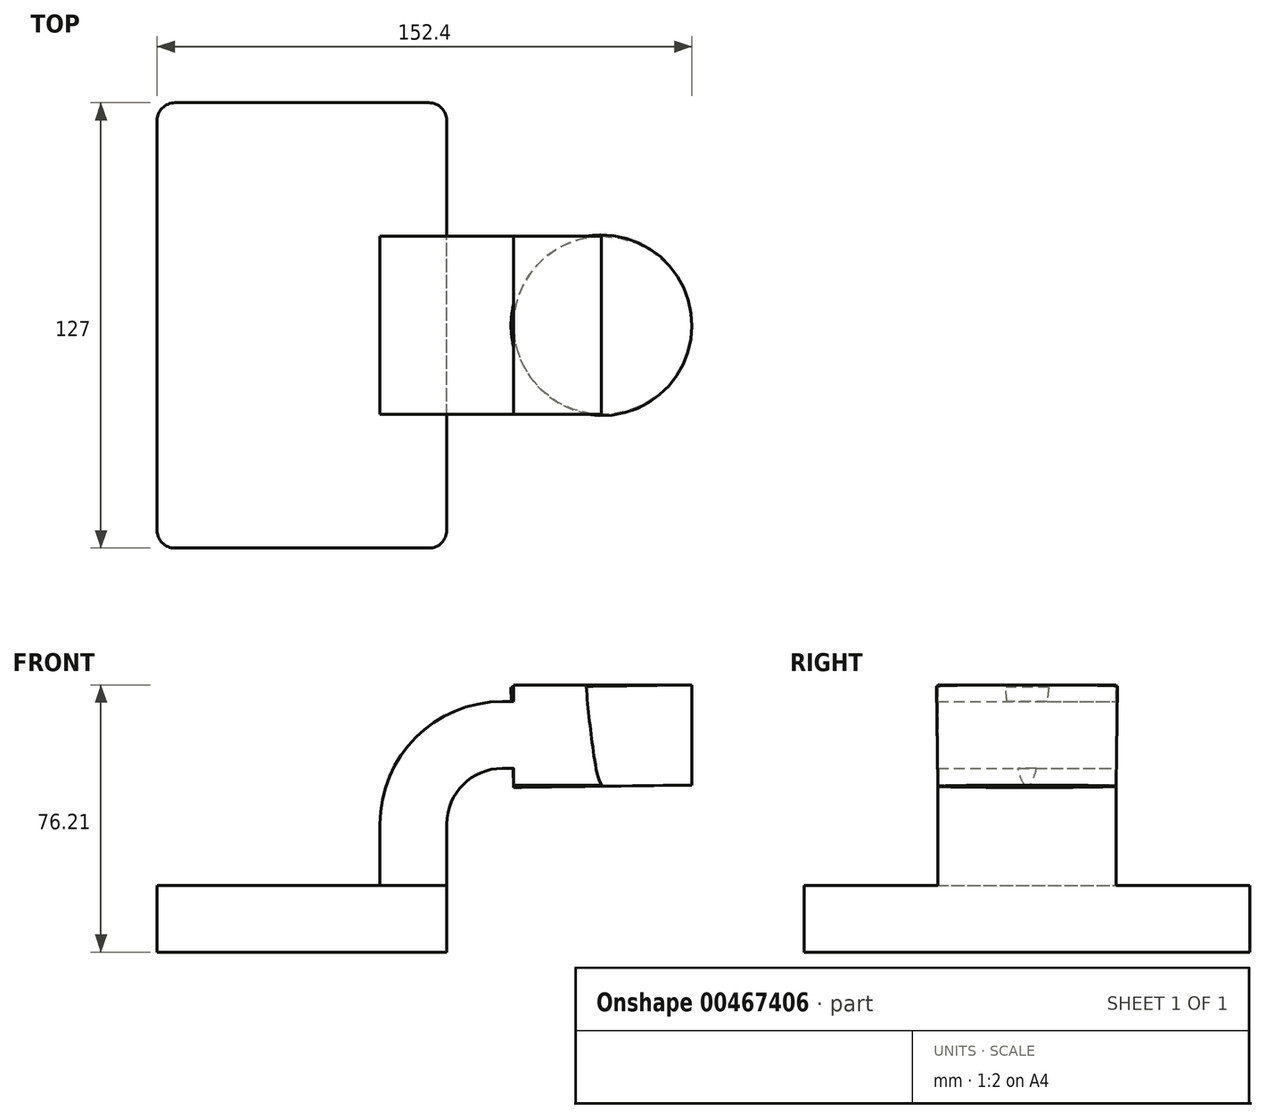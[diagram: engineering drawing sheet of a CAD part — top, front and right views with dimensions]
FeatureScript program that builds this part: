
annotation { "Feature Type Name" : "Feature", "Feature Type Description" : "" }
export const myFeature = defineFeature(function(context is Context, id is Id, definition is map)
    precondition{}
    {
        {
            var Q0;
            Q0=qCreatedBy(makeId("Front.planeOp"),FACE);
            var sketch = newSketch(context, id + "F0", { "sketchPlane" : qUnion([Q0])});
            skLineSegment(sketch, "E0.bottom", {"start": v(-41.27, -9.53) * mm, "end": v(41.28, -9.53) * mm});
            skLineSegment(sketch, "E0.top", {"start": v(-41.28, 9.53) * mm, "end": v(41.28, 9.53) * mm});
            skLineSegment(sketch, "E0.left", {"start": v(-41.28, -9.53) * mm, "end": v(-41.28, 9.53) * mm});
            skLineSegment(sketch, "E0.right", {"start": v(41.28, -9.53) * mm, "end": v(41.28, 9.52) * mm});
            skPoint(sketch, "E0.middle", {"position": v(0, 0) * mm});
            skLineSegment(sketch, "E1.bottom", {"start": v(60.33, 38.1) * mm, "end": v(111.12, 38.1) * mm});
            skLineSegment(sketch, "E1.top", {"start": v(60.33, 66.67) * mm, "end": v(111.12, 66.67) * mm});
            skLineSegment(sketch, "E1.left", {"start": v(60.33, 38.1) * mm, "end": v(60.33, 66.67) * mm});
            skLineSegment(sketch, "E1.right", {"start": v(111.12, 38.1) * mm, "end": v(111.12, 66.67) * mm});
            skPoint(sketch, "E1.middle", {"position": v(85.72, 52.39) * mm});
            skLineSegment(sketch, "E2", {"start": v(41.28, 9.52) * mm, "end": v(41.28, 27) * mm});
            skArc(sketch, "E3", {"start": v(41.27, 27) * mm, "mid": v(45.92, 38.23) * mm, "end": v(57.15, 42.88) * mm});
            skLineSegment(sketch, "E4", {"start": v(57.15, 42.88) * mm, "end": v(85.35, 42.88) * mm});
            skLineSegment(sketch, "E5.0", {"start": v(57.15, 61.93) * mm, "end": v(85.35, 61.93) * mm});
            skArc(sketch, "E5.1", {"start": v(22.22, 27) * mm, "mid": v(32.45, 51.7) * mm, "end": v(57.15, 61.93) * mm});
            skLineSegment(sketch, "E5.2", {"start": v(22.22, 9.52) * mm, "end": v(22.22, 27) * mm});
            skLineSegment(sketch, "E6", {"start": v(85.72, 38.1) * mm, "end": v(85.35, 66.67) * mm});
            skFitSpline(sketch, "E7", {"points": [v(-41.28, 9.53) * mm, v(57.15, 61.93) * mm], "startDerivative": vector(3.42, 95.3) * mm, "endDerivative": vector(138.23, -0.37) * mm});
            skSolve(sketch);
        }
        {
            var Q0;
            Q0=makeQuery(id+"F0.imprint","IMPRINT",FACE,{"disambiguationData":[TD([[makeQuery(id+"F0.imprint","IMPRINT",EDGE,{"derivedFrom":sQuery(id+"F0.wireOp",EDGE,"E0.bottom")}),1.0]])]});
            extrude(context, id + "F1", {"entities" : qUnion([Q0]), "endBound" : BoundingType.SYMMETRIC, "depth" : 127 * mm});
        }
        {
            var Q0;
            {var subQ1=sQuery(id+"F0.wireOp",EDGE,"E2");Q0=makeQuery(id+"F0.imprint","IMPRINT",FACE,{"disambiguationData":[TD([[makeQuery(id+"F0.imprint","IMPRINT",EDGE,{"derivedFrom":subQ1}),1.0]])]});}
            var Q1;
            {var subQ6=sQuery(id+"F0.wireOp",EDGE,"E6");Q1=makeQuery(id+"F0.imprint","IMPRINT",FACE,{"disambiguationData":[TD([[makeQuery(id+"F0.imprint","IMPRINT",EDGE,{"derivedFrom":subQ6}),1.0]])]});}
            extrude(context, id + "F2", {"entities" : qUnion([Q0, Q1]), "operationType" : NewBodyOperationType.ADD, "endBound" : BoundingType.SYMMETRIC, "depth" : 50.8 * mm});
        }
        {
            var Q0;
            Q0=makeQuery(id+"F0.imprint","IMPRINT",FACE,{"disambiguationData":[TD([[makeQuery(id+"F0.imprint","IMPRINT",EDGE,{"derivedFrom":sQuery(id+"F0.wireOp",EDGE,"E5.1")}),1.0]])]});
            extrude(context, id + "F3", {"entities" : qUnion([Q0]), "operationType" : NewBodyOperationType.ADD, "endBound" : BoundingType.SYMMETRIC, "depth" : 15.88 * mm});
        }
        {
            var Q0;
            {var subQ0=sQuery(id+"F0.wireOp",EDGE,"E1.right");Q0=makeQuery(id+"F0.imprint","IMPRINT",FACE,{"disambiguationData":[TD([[makeQuery(id+"F0.imprint","IMPRINT",EDGE,{"derivedFrom":subQ0}),1.0]])]});}
            var Q1;
            Q1=sQuery(id+"F0.wireOp",EDGE,"E6");
            revolve(context, id + "F4", {"operationType" : NewBodyOperationType.ADD, "entities" : qUnion([Q0]), "axis" : qUnion([Q1]), "revolveType" : RevolveType.FULL});
        }
        {
            var Q0;
            Q0=makeQuery(id+"F1.opExtrude","CAP_EDGE",EDGE,{"disambiguationData":[OSD([sQuery(id+"F0.wireOp",EDGE,"E0.right")])],"isStart":false});
            var Q1;
            Q1=makeQuery(id+"F1.opExtrude","CAP_EDGE",EDGE,{"disambiguationData":[OSD([sQuery(id+"F0.wireOp",EDGE,"E0.right")])],"isStart":true});
            var Q2;
            Q2=makeQuery(id+"F1.opExtrude","CAP_EDGE",EDGE,{"disambiguationData":[OSD([sQuery(id+"F0.wireOp",EDGE,"E0.left")])],"isStart":true});
            var Q3;
            Q3=makeQuery(id+"F1.opExtrude","CAP_EDGE",EDGE,{"disambiguationData":[OSD([sQuery(id+"F0.wireOp",EDGE,"E0.left")])],"isStart":false});
            fillet(context, id + "F5", {"entities" : qUnion([Q0, Q1, Q2, Q3]), "radius" : 5.08 * mm, "tangentPropagation" : true, "allowEdgeOverflow" : false});
        }
    });
